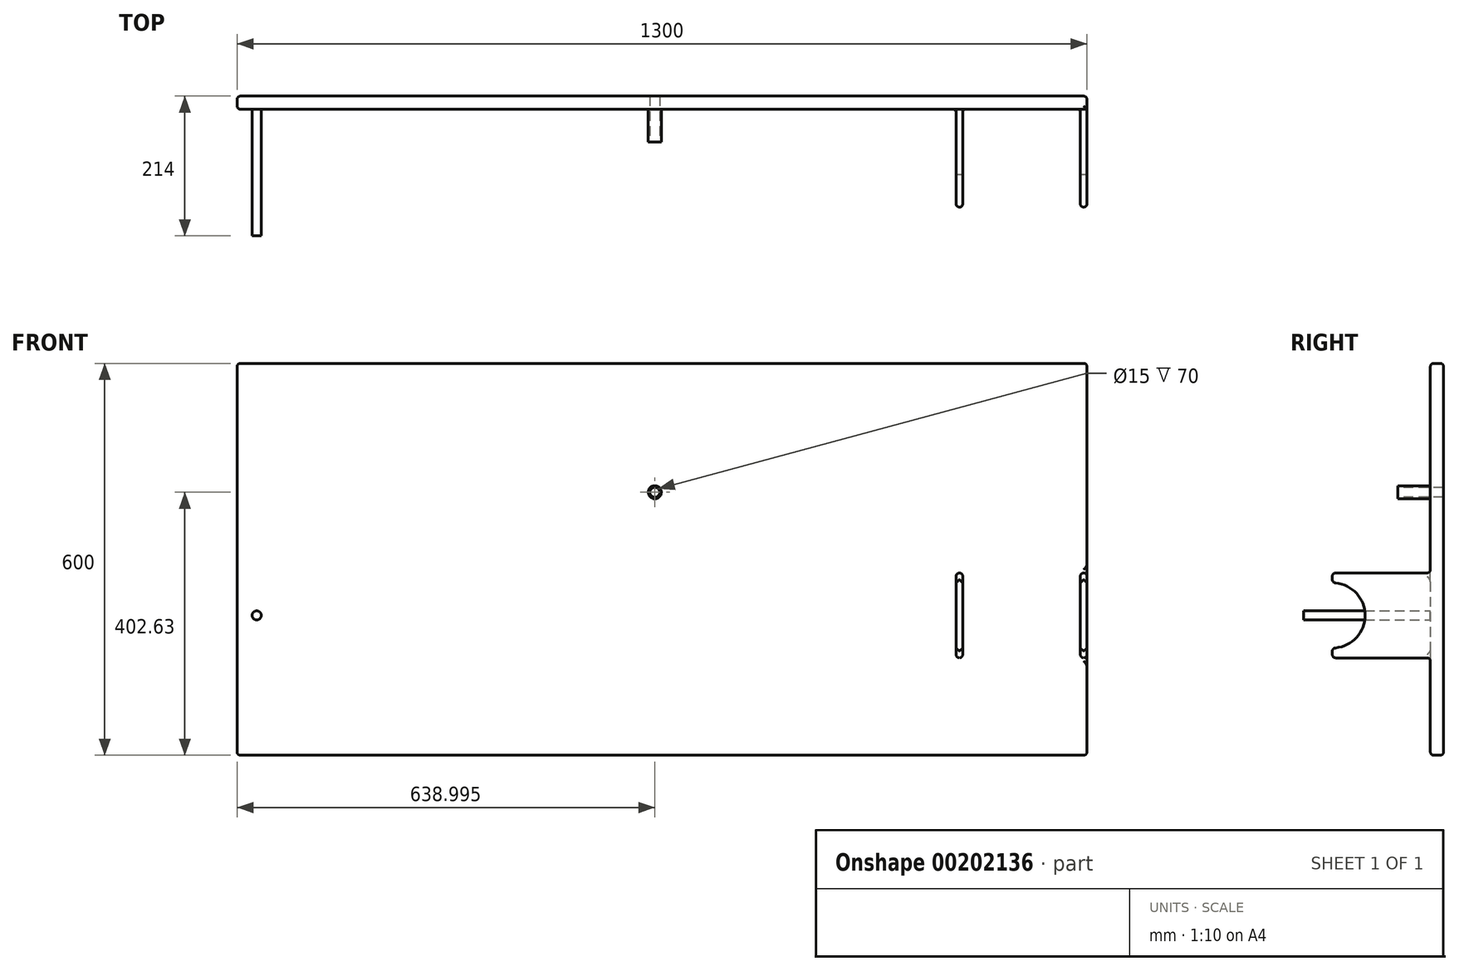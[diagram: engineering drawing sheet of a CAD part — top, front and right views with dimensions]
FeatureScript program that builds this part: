
annotation { "Feature Type Name" : "Feature", "Feature Type Description" : "" }
export const myFeature = defineFeature(function(context is Context, id is Id, definition is map)
    precondition{}
    {
        {
            var Q0;
            Q0=qCreatedBy(makeId("Front.planeOp"),FACE);
            var sketch = newSketch(context, id + "F0", { "sketchPlane" : qUnion([Q0])});
            skLineSegment(sketch, "E0.bottom", {"start": v(-340.11, -214.13) * mm, "end": v(959.89, -214.13) * mm});
            skLineSegment(sketch, "E0.top", {"start": v(-340.11, 385.87) * mm, "end": v(959.89, 385.87) * mm});
            skLineSegment(sketch, "E0.left", {"start": v(-340.11, -214.13) * mm, "end": v(-340.11, 385.87) * mm});
            skLineSegment(sketch, "E0.right", {"start": v(959.89, -214.13) * mm, "end": v(959.89, 385.87) * mm});
            skLineSegment(sketch, "E1", {"start": v(-340.11, 0) * mm, "end": v(959.89, 0) * mm});
            skSolve(sketch);
        }
        {
            var Q0;
            Q0 = qSketchRegion(id + "F0", true);
            extrude(context, id + "F1", {"entities" : qUnion([Q0]), "depth" : 20 * mm});
        }
        {
            var Q0;
            Q0=makeQuery(id+"F1.opExtrude","CAP_FACE",FACE,{"disambiguationData":[OSD([sQuery(id+"F0.wireOp",EDGE,"E0.bottom"),sQuery(id+"F0.wireOp",EDGE,"E0.top"),sQuery(id+"F0.wireOp",EDGE,"E0.left"),sQuery(id+"F0.wireOp",EDGE,"E0.right")])],"isStart":false});
            var sketch = newSketch(context, id + "F2", { "sketchPlane" : qUnion([Q0])});
            skLineSegment(sketch, "E2.bottom", {"start": v(759.89, 65) * mm, "end": v(769.89, 65) * mm});
            skLineSegment(sketch, "E2.top", {"start": v(759.89, -65) * mm, "end": v(769.89, -65) * mm});
            skLineSegment(sketch, "E2.left", {"start": v(759.89, 65) * mm, "end": v(759.89, -65) * mm});
            skLineSegment(sketch, "E2.right", {"start": v(769.89, 65) * mm, "end": v(769.89, -65) * mm});
            skLineSegment(sketch, "E3.bottom", {"start": v(949.89, 65) * mm, "end": v(959.89, 65) * mm});
            skLineSegment(sketch, "E3.top", {"start": v(949.89, -65) * mm, "end": v(959.89, -65) * mm});
            skLineSegment(sketch, "E3.left", {"start": v(949.89, 65) * mm, "end": v(949.89, -65) * mm});
            skLineSegment(sketch, "E3.right", {"start": v(959.89, 65) * mm, "end": v(959.89, -65) * mm});
            skLineSegment(sketch, "E4", {"start": v(764.89, 65) * mm, "end": v(764.89, -65) * mm});
            skLineSegment(sketch, "E5", {"start": v(954.89, 65) * mm, "end": v(954.89, -65) * mm});
            skLineSegment(sketch, "E6", {"start": v(769.89, 0) * mm, "end": v(949.89, 0) * mm});
            skSolve(sketch);
        }
        {
            var Q0;
            Q0 = qSketchRegion(id + "F2", true);
            extrude(context, id + "F3", {"entities" : qUnion([Q0]), "operationType" : NewBodyOperationType.ADD, "depth" : 150 * mm});
        }
        {
            var Q0;
            Q0=makeQuery(id+"F3.boolean.opBoolean","MERGE",FACE,{"derivedFrom":[makeQuery(id+"F1.opExtrude","SWEPT_FACE",FACE,{"disambiguationData":[OSD([sQuery(id+"F0.wireOp",EDGE,"E0.right")])]}),makeQuery(id+"F3.opExtrude","SWEPT_FACE",FACE,{"disambiguationData":[OSD([sQuery(id+"F2.wireOp",EDGE,"E3.right")])]})]});
            var sketch = newSketch(context, id + "F4", { "sketchPlane" : qUnion([Q0])});
            skCircle(sketch, "E7", {"center": v(-170, 0) * mm, "radius": 50 * mm});
            skPoint(sketch, "E7.centerSnap0", {"position": v(-170, 0) * mm});
            skSolve(sketch);
        }
        {
            var Q0;
            Q0 = qSketchRegion(id + "F4", true);
            extrude(context, id + "F5", {"entities" : qUnion([Q0]), "operationType" : NewBodyOperationType.REMOVE, "oppositeDirection" : true, "depth" : 2015 * mm});
        }
        {
            var Q0;
            {var subQ0=sQuery(id+"F2.wireOp",EDGE,"E2.top");var subQ1=sQuery(id+"F2.wireOp",EDGE,"E2.left");var subQ2=sQuery(id+"F2.wireOp",EDGE,"E2.right");Q0=makeQuery(id+"F5.boolean.opBoolean","SPLIT",FACE,{"disambiguationData":[TD([makeQuery(id+"F3.opExtrude","SWEPT_FACE",FACE,{"disambiguationData":[OSD([subQ0])]})])],"derivedFrom":makeQuery(id+"F3.opExtrude","CAP_FACE",FACE,{"disambiguationData":[OSD([sQuery(id+"F2.wireOp",EDGE,"E2.bottom"),subQ0,subQ1,subQ2])],"isStart":false})});}
            var Q1;
            {var subQ0=sQuery(id+"F2.wireOp",EDGE,"E2.bottom");var subQ1=sQuery(id+"F2.wireOp",EDGE,"E2.left");var subQ2=sQuery(id+"F2.wireOp",EDGE,"E2.right");Q1=makeQuery(id+"F5.boolean.opBoolean","SPLIT",FACE,{"disambiguationData":[TD([makeQuery(id+"F3.opExtrude","SWEPT_FACE",FACE,{"disambiguationData":[OSD([subQ0])]})])],"derivedFrom":makeQuery(id+"F3.opExtrude","CAP_FACE",FACE,{"disambiguationData":[OSD([subQ0,sQuery(id+"F2.wireOp",EDGE,"E2.top"),subQ1,subQ2])],"isStart":false})});}
            var Q2;
            Q2=makeQuery(id+"F3.opExtrude","SWEPT_FACE",FACE,{"disambiguationData":[OSD([sQuery(id+"F2.wireOp",EDGE,"E2.top")])]});
            var Q3;
            Q3=makeQuery(id+"F3.opExtrude","SWEPT_FACE",FACE,{"disambiguationData":[OSD([sQuery(id+"F2.wireOp",EDGE,"E2.bottom")])]});
            var Q4;
            {var subQ0=sQuery(id+"F2.wireOp",EDGE,"E3.right");var subQ1=sQuery(id+"F2.wireOp",EDGE,"E3.left");var subQ2=sQuery(id+"F2.wireOp",EDGE,"E3.bottom");Q4=makeQuery(id+"F5.boolean.opBoolean","SPLIT",FACE,{"disambiguationData":[TD([makeQuery(id+"F3.opExtrude","SWEPT_FACE",FACE,{"disambiguationData":[OSD([subQ2])]})])],"derivedFrom":makeQuery(id+"F3.opExtrude","CAP_FACE",FACE,{"disambiguationData":[OSD([subQ2,sQuery(id+"F2.wireOp",EDGE,"E3.top"),subQ1,subQ0])],"isStart":false})});}
            var Q5;
            {var subQ0=sQuery(id+"F2.wireOp",EDGE,"E3.right");var subQ1=sQuery(id+"F2.wireOp",EDGE,"E3.left");var subQ2=sQuery(id+"F2.wireOp",EDGE,"E3.top");Q5=makeQuery(id+"F5.boolean.opBoolean","SPLIT",FACE,{"disambiguationData":[TD([makeQuery(id+"F3.opExtrude","SWEPT_FACE",FACE,{"disambiguationData":[OSD([subQ2])]})])],"derivedFrom":makeQuery(id+"F3.opExtrude","CAP_FACE",FACE,{"disambiguationData":[OSD([sQuery(id+"F2.wireOp",EDGE,"E3.bottom"),subQ2,subQ1,subQ0])],"isStart":false})});}
            var Q6;
            Q6=makeQuery(id+"F3.opExtrude","SWEPT_FACE",FACE,{"disambiguationData":[OSD([sQuery(id+"F2.wireOp",EDGE,"E3.top")])]});
            var Q7;
            Q7=makeQuery(id+"F3.opExtrude","SWEPT_FACE",FACE,{"disambiguationData":[OSD([sQuery(id+"F2.wireOp",EDGE,"E3.bottom")])]});
            var Q8;
            Q8=makeQuery(id+"F1.opExtrude","CAP_EDGE",EDGE,{"disambiguationData":[OSD([sQuery(id+"F0.wireOp",EDGE,"E0.top")])],"isStart":true});
            var Q9;
            Q9=makeQuery(id+"F1.opExtrude","SWEPT_FACE",FACE,{"disambiguationData":[OSD([sQuery(id+"F0.wireOp",EDGE,"E0.top")])]});
            var Q10;
            Q10=makeQuery(id+"F1.opExtrude","SWEPT_FACE",FACE,{"disambiguationData":[OSD([sQuery(id+"F0.wireOp",EDGE,"E0.bottom")])]});
            var Q11;
            Q11=makeQuery(id+"F1.opExtrude","CAP_FACE",FACE,{"disambiguationData":[OSD([sQuery(id+"F0.wireOp",EDGE,"E0.bottom"),sQuery(id+"F0.wireOp",EDGE,"E0.top"),sQuery(id+"F0.wireOp",EDGE,"E0.left"),sQuery(id+"F0.wireOp",EDGE,"E0.right")])],"isStart":true});
            var Q12;
            Q12=makeQuery(id+"F1.opExtrude","SWEPT_FACE",FACE,{"disambiguationData":[OSD([sQuery(id+"F0.wireOp",EDGE,"E0.left")])]});
            fillet(context, id + "F6", {"entities" : qUnion([Q0, Q1, Q2, Q3, Q4, Q5, Q6, Q7, Q8, Q9, Q10, Q11, Q12]), "radius" : 5 * mm, "tangentPropagation" : true, "allowEdgeOverflow" : false});
        }
        {
            var Q0;
            Q0=makeQuery(id+"F1.opExtrude","CAP_FACE",FACE,{"disambiguationData":[OSD([sQuery(id+"F0.wireOp",EDGE,"E0.bottom"),sQuery(id+"F0.wireOp",EDGE,"E0.top"),sQuery(id+"F0.wireOp",EDGE,"E0.left"),sQuery(id+"F0.wireOp",EDGE,"E0.right")])],"isStart":false});
            var sketch = newSketch(context, id + "F7", { "sketchPlane" : qUnion([Q0])});
            skCircle(sketch, "E8", {"center": v(298.89, 188.5) * mm, "radius": 7.5 * mm});
            skCircle(sketch, "E9", {"center": v(298.89, 188.5) * mm, "radius": 10 * mm});
            skSolve(sketch);
        }
        {
            var Q0;
            Q0=makeQuery(id+"F7.imprint","IMPRINT",FACE,{"disambiguationData":[TD([[makeQuery(id+"F7.imprint","IMPRINT",EDGE,{"derivedFrom":sQuery(id+"F7.wireOp",EDGE,"E8")}),1.0]])]});
            extrude(context, id + "F8", {"entities" : qUnion([Q0]), "operationType" : NewBodyOperationType.REMOVE, "endBound" : BoundingType.THROUGH_ALL, "oppositeDirection" : true, "depth" : 25 * mm});
        }
        {
            var Q0;
            Q0 = qSketchRegion(id + "F7", true);
            extrude(context, id + "F9", {"entities" : qUnion([Q0]), "operationType" : NewBodyOperationType.ADD, "depth" : 50 * mm});
        }
        {
            var Q0;
            Q0=makeQuery(id+"F1.opExtrude","CAP_FACE",FACE,{"disambiguationData":[OSD([sQuery(id+"F0.wireOp",EDGE,"E0.bottom"),sQuery(id+"F0.wireOp",EDGE,"E0.top"),sQuery(id+"F0.wireOp",EDGE,"E0.left"),sQuery(id+"F0.wireOp",EDGE,"E0.right")])],"isStart":false});
            var sketch = newSketch(context, id + "F10", { "sketchPlane" : qUnion([Q0])});
            skCircle(sketch, "E10", {"center": v(-310.11, 0) * mm, "radius": 7 * mm});
            skSolve(sketch);
        }
        {
            var Q0;
            Q0 = qSketchRegion(id + "F10", true);
            extrude(context, id + "F11", {"entities" : qUnion([Q0]), "operationType" : NewBodyOperationType.ADD, "depth" : 194 * mm});
        }
    });
